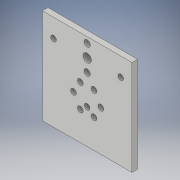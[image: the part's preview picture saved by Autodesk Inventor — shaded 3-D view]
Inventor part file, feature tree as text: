
AUTODESK INVENTOR PART (.ipt)
format: ipt  version: 2019 (Build 230136000, 136)  size: 158,720 bytes
history: native  units: in
note: dims shown in document units (in); Inventor stores cm internally (conversion verified against a paired STEP export)
features: sketch x7, hole x6, extrude x1
ambient origin geometry x8: Origin, YZ Plane, XZ Plane, XY Plane, X Axis, Y Axis, Z Axis, Center Point
bodies: Solid1 (feature_tree)
feature tree (14):
  extrude  "Extrusion1"  Depth=4.25in
  hole  "Hole1"  [1 undecoded]
  hole  "Hole2"  [1 undecoded]
  hole  "Hole3"  [1 undecoded]
  hole  "Hole5"  [1 undecoded]
  hole  "Hole6"  [1 undecoded]
  hole  "Hole8"  [1 undecoded]
  sketch  "Sketch1"  dims[d0=4.0in d1=4.25in]
  sketch  "Sketch2"  dims[d2=0.25in d3=0.0in]
  sketch  "Sketch3"  dims[d4=0.375in d5=0.75in d6=0.375in d7=0.25in d8=0.5635in d9=0.75in d10=0.8108in d12=0.5in]
  sketch  "Sketch4"  dims[d15=3.0in]
  sketch  "Sketch6"  dims[d21=0.125in d22=0.75in d23=0.25in d24=0.125in d25=0.5635in d26=0.75in d27=0.8108in d31=0.82in]
  sketch  "Sketch7"  dims[d32=0.25in d33=0.75in d34=0.375in d35=0.25in d36=0.5635in d37=0.75in d38=0.8108in d39=1.8898in]
  sketch  "Sketch8"  dims[d52=1.125in d53=0.5625in d54=0.15in d55=0.75in d56=0.25in d57=0.02in d58=90.0deg d59=0.75in d60=0.8108in d61=0.15in d62=0.75in d63=0.281in d64=0.138in d65=90.0deg d66=0.75in d67=0.8108in d68=1.2205in d69=0.2756in d77=2.3622in d79=360.0deg d81=0.134in d82=0.75in d83=0.256in d84=0.118in d85=0.5635in d86=0.484in d87=0.8108in]
note: 6 required parameter values undecoded (feature->parameter linkage not recoverable at this tier; creation-order binding heuristic only, values carry confidence <= 0.55)
